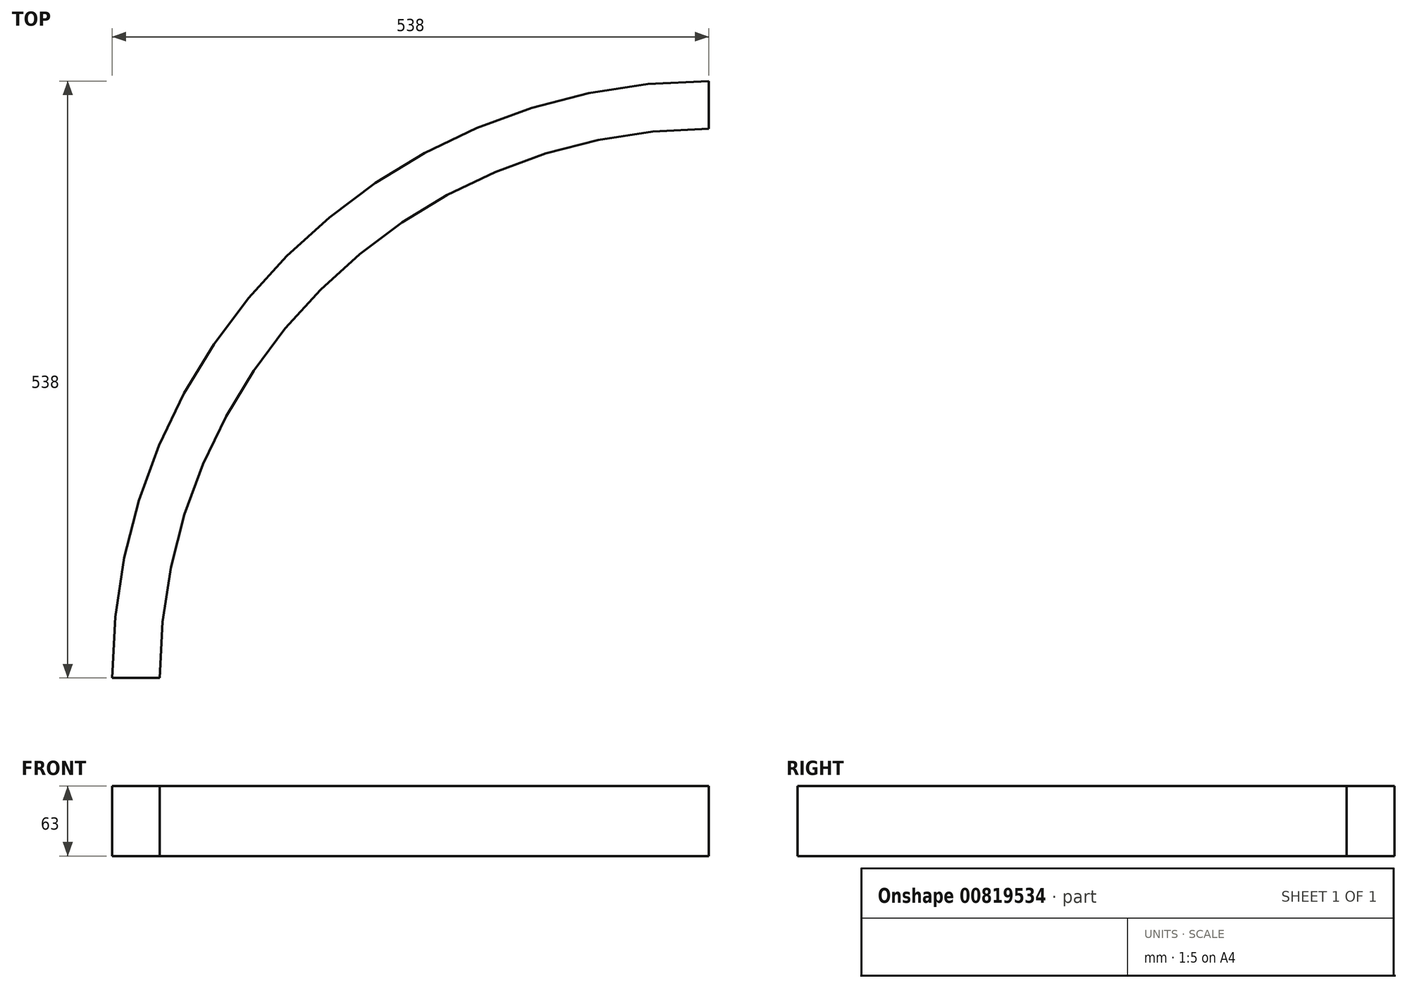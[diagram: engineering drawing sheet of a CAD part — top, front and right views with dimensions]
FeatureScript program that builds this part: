
annotation { "Feature Type Name" : "Feature", "Feature Type Description" : "" }
export const myFeature = defineFeature(function(context is Context, id is Id, definition is map)
    precondition{}
    {
        {
            var Q0;
            Q0=qCreatedBy(makeId("Top.planeOp"),FACE);
            var sketch = newSketch(context, id + "F0", { "sketchPlane" : qUnion([Q0])});
            skArc(sketch, "E0", {"start": v(0, 495) * mm, "mid": v(-350.02, 350.02) * mm, "end": v(-495, 0) * mm});
            skLineSegment(sketch, "E1", {"start": v(-495, 0) * mm, "end": v(-516.5, 0) * mm});
            skPoint(sketch, "E2", {"position": v(-516.5, 0) * mm});
            skPoint(sketch, "E3", {"position": v(-495, 0) * mm});
            skLineSegment(sketch, "E4", {"start": v(0, 495) * mm, "end": v(0, 516.5) * mm});
            skPoint(sketch, "E5", {"position": v(0, 495) * mm});
            skLineSegment(sketch, "E6", {"start": v(-495, 0) * mm, "end": v(-538, 0) * mm});
            skArc(sketch, "E7", {"start": v(0, 538) * mm, "mid": v(-380.42, 380.42) * mm, "end": v(-538, 0) * mm});
            skPoint(sketch, "E8", {"position": v(-538, 0) * mm});
            skLineSegment(sketch, "E9", {"start": v(0, 495) * mm, "end": v(0, 538) * mm});
            skPoint(sketch, "E10", {"position": v(0, 538) * mm});
            skSolve(sketch);
        }
        {
            var Q0;
            {var subQ0=sQuery(id+"F0.wireOp",EDGE,"E0");Q0=makeQuery(id+"F0.imprint","IMPRINT",FACE,{"disambiguationData":[TD([[makeQuery(id+"F0.imprint","IMPRINT",EDGE,{"derivedFrom":subQ0}),-1.0]])]});}
            extrude(context, id + "F1", {"entities" : qUnion([Q0]), "depth" : 63 * mm, "offsetDistance" : 25 * mm});
        }
    });
